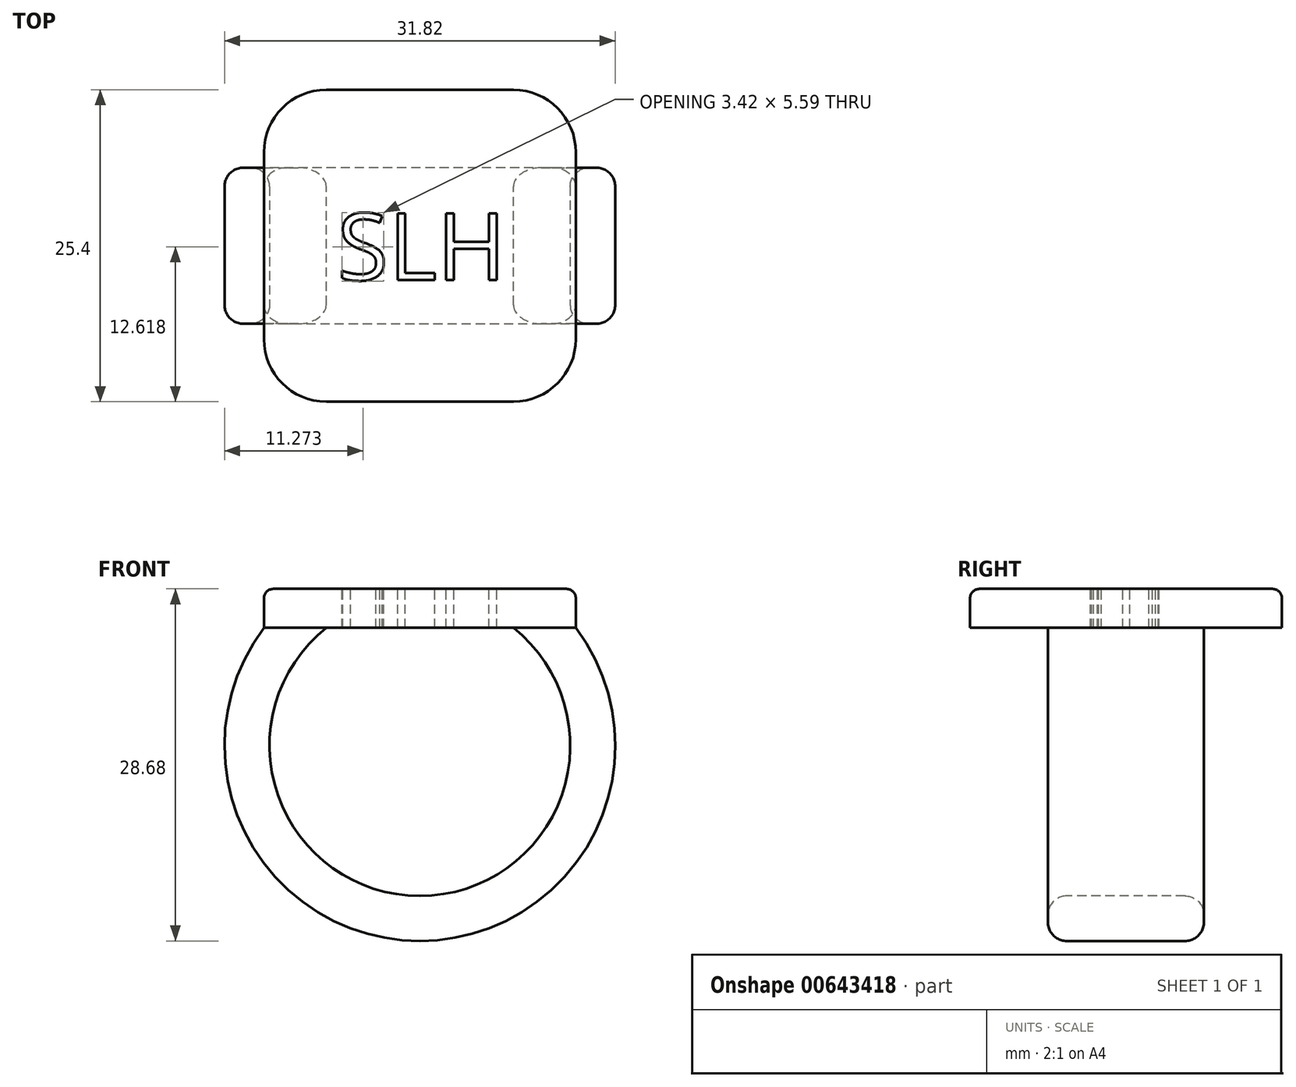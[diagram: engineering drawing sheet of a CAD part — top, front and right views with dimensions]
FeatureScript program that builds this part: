
annotation { "Feature Type Name" : "Feature", "Feature Type Description" : "" }
export const myFeature = defineFeature(function(context is Context, id is Id, definition is map)
    precondition{}
    {
        {
            var Q0;
            Q0=qCreatedBy(makeId("Top.planeOp"),FACE);
            var sketch = newSketch(context, id + "F0", { "sketchPlane" : qUnion([Q0])});
            skLineSegment(sketch, "E0.bottom", {"start": v(-12.7, 12.7) * mm, "end": v(12.7, 12.7) * mm});
            skLineSegment(sketch, "E0.top", {"start": v(-12.7, -12.7) * mm, "end": v(12.7, -12.7) * mm});
            skLineSegment(sketch, "E0.left", {"start": v(-12.7, 12.7) * mm, "end": v(-12.7, -12.7) * mm});
            skLineSegment(sketch, "E0.right", {"start": v(12.7, 12.7) * mm, "end": v(12.7, -12.7) * mm});
            skPoint(sketch, "E0.middle", {"position": v(0, 0) * mm});
            skSolve(sketch);
        }
        {
            var Q0;
            Q0 = qSketchRegion(id + "F0", true);
            extrude(context, id + "F1", {"entities" : qUnion([Q0]), "depth" : 3.17 * mm, "offsetDistance" : 25 * mm});
        }
        {
            var Q0;
            Q0=qCreatedBy(makeId("Front.planeOp"),FACE);
            var sketch = newSketch(context, id + "F2", { "sketchPlane" : qUnion([Q0])});
            skArc(sketch, "E1", {"start": v(-10.16, 0) * mm, "mid": v(0, -23.56) * mm, "end": v(10.16, 0) * mm});
            skSolve(sketch);
        }
        {
            var Q0;
            Q0=makeQuery(id+"F1.opExtrude","CAP_FACE",FACE,{"disambiguationData":[OSD([sQuery(id+"F0.wireOp",EDGE,"E0.bottom"),sQuery(id+"F0.wireOp",EDGE,"E0.top"),sQuery(id+"F0.wireOp",EDGE,"E0.left"),sQuery(id+"F0.wireOp",EDGE,"E0.right")])],"isStart":true});
            var sketch = newSketch(context, id + "F3", { "sketchPlane" : qUnion([Q0])});
            skLineSegment(sketch, "E2.bottom", {"start": v(-12.7, 6.35) * mm, "end": v(-7.62, 6.35) * mm});
            skLineSegment(sketch, "E2.top", {"start": v(-12.7, -6.35) * mm, "end": v(-7.62, -6.35) * mm});
            skLineSegment(sketch, "E2.left", {"start": v(-12.7, 6.35) * mm, "end": v(-12.7, -6.35) * mm});
            skLineSegment(sketch, "E2.right", {"start": v(-7.62, 6.35) * mm, "end": v(-7.62, -6.35) * mm});
            skPoint(sketch, "E2.middle", {"position": v(-10.16, 0) * mm});
            skSolve(sketch);
        }
        {
            var Q0;
            Q0 = qSketchRegion(id + "F3", true);
            var Q1;
            Q1 = qConstructionFilter(qBodyType(qCreatedBy(id + "F2" ,EDGE), BodyType.WIRE), ConstructionObject.NO);
            sweep(context, id + "F4", {"operationType" : NewBodyOperationType.ADD, "profiles" : qUnion([Q0]), "path" : qUnion([Q1])});
        }
        {
            var Q0;
            Q0=qCreatedBy(makeId("Front.planeOp"),FACE);
            var sketch = newSketch(context, id + "F5", { "sketchPlane" : qUnion([Q0])});
            skLineSegment(sketch, "E3.1", {"start": v(10.01, -2.54) * mm, "end": v(10.16, 0) * mm});
            skArc(sketch, "E3.2", {"start": v(10.01, -2.54) * mm, "mid": v(8.9, -1.18) * mm, "end": v(7.62, 0) * mm});
            skLineSegment(sketch, "E4.trimOffspring", {"start": v(7.62, 0) * mm, "end": v(10.16, 0) * mm});
            skPoint(sketch, "E5.0.3.start.orphan", {"position": v(-12.7, 3.18) * mm});
            skPoint(sketch, "E5.0.1.end.orphan", {"position": v(12.7, 3.18) * mm});
            skPoint(sketch, "E6.orphan", {"position": v(12.7, 0) * mm});
            skPoint(sketch, "E3.0.end.orphan", {"position": v(-7.62, 0) * mm});
            skPoint(sketch, "E3.0.start.orphan", {"position": v(-12.7, 0) * mm});
            skSolve(sketch);
        }
        {
            var Q0;
            Q0 = qSketchRegion(id + "F5", true);
            var Q1;
            Q1=makeQuery(id+"F4.opSweep","SWEPT_FACE",FACE,{"disambiguationData":[OSD([sQuery(id+"F2.wireOp",EDGE,"E1"),sQuery(id+"F3.wireOp",EDGE,"E2.bottom")])]});
            var Q2;
            Q2=makeQuery(id+"F4.opSweep","SWEPT_FACE",FACE,{"disambiguationData":[OSD([sQuery(id+"F2.wireOp",EDGE,"E1"),sQuery(id+"F3.wireOp",EDGE,"E2.top")])]});
            extrude(context, id + "F6", {"entities" : qUnion([Q0]), "operationType" : NewBodyOperationType.ADD, "endBound" : BoundingType.UP_TO_SURFACE, "depth" : 25.4 * mm, "endBoundEntityFace" : qUnion([Q1]), "offsetDistance" : 25.4 * mm, "hasSecondDirection" : true, "secondDirectionBound" : SecondDirectionBoundingType.UP_TO_SURFACE, "secondDirectionOppositeDirection" : true, "secondDirectionDepth" : 25.4 * mm, "secondDirectionBoundEntityFace" : qUnion([Q2])});
        }
        {
            var Q0;
            Q0=makeQuery(id+"F1.opExtrude","SWEPT_EDGE",EDGE,{"disambiguationData":[OSD([sQuery(id+"F0.wireOp",EDGE,"E0.top"),sQuery(id+"F0.wireOp",EDGE,"E0.left")])]});
            var Q1;
            Q1=makeQuery(id+"F1.opExtrude","SWEPT_EDGE",EDGE,{"disambiguationData":[OSD([sQuery(id+"F0.wireOp",EDGE,"E0.top"),sQuery(id+"F0.wireOp",EDGE,"E0.right")])]});
            var Q2;
            Q2=makeQuery(id+"F1.opExtrude","SWEPT_EDGE",EDGE,{"disambiguationData":[OSD([sQuery(id+"F0.wireOp",EDGE,"E0.bottom"),sQuery(id+"F0.wireOp",EDGE,"E0.right")])]});
            var Q3;
            Q3=makeQuery(id+"F1.opExtrude","SWEPT_EDGE",EDGE,{"disambiguationData":[OSD([sQuery(id+"F0.wireOp",EDGE,"E0.bottom"),sQuery(id+"F0.wireOp",EDGE,"E0.left")])]});
            fillet(context, id + "F7", {"entities" : qUnion([Q0, Q1, Q2, Q3]), "radius" : 5.08 * mm, "tangentPropagation" : true, "allowEdgeOverflow" : false});
        }
        {
            var Q0;
            {var subQ0=sQuery(id+"F3.wireOp",EDGE,"E2.top");var subQ1=sQuery(id+"F2.wireOp",EDGE,"E1");Q0=makeQuery(id+"F6.boolean.opBoolean","MERGE",EDGE,{"derivedFrom":[makeQuery(id+"F4.opSweep","SWEPT_EDGE",EDGE,{"disambiguationData":[OSD([subQ1,subQ0,sQuery(id+"F3.wireOp",EDGE,"E2.right")])]}),makeQuery(id+"F6.opExtrude","TWEAK_EDGE",EDGE,{"derivedFrom":[makeQuery(id+"F4.opSweep","SWEPT_FACE",FACE,{"disambiguationData":[OSD([subQ1,subQ0])]}),makeQuery(id+"F5.imprint","IMPRINT",EDGE,{"derivedFrom":sQuery(id+"F5.wireOp",EDGE,"E3.2")})]})]});}
            var Q1;
            Q1=makeQuery(id+"F4.opSweep","SWEPT_EDGE",EDGE,{"disambiguationData":[OSD([sQuery(id+"F0.wireOp",EDGE,"E0.left"),sQuery(id+"F2.wireOp",EDGE,"E1"),sQuery(id+"F3.wireOp",EDGE,"E2.top"),sQuery(id+"F3.wireOp",EDGE,"E2.left")])]});
            var Q2;
            {var subQ0=sQuery(id+"F3.wireOp",EDGE,"E2.bottom");var subQ1=sQuery(id+"F2.wireOp",EDGE,"E1");Q2=makeQuery(id+"F6.boolean.opBoolean","MERGE",EDGE,{"derivedFrom":[makeQuery(id+"F4.opSweep","SWEPT_EDGE",EDGE,{"disambiguationData":[OSD([subQ1,subQ0,sQuery(id+"F3.wireOp",EDGE,"E2.right")])]}),makeQuery(id+"F6.opExtrude","TWEAK_EDGE",EDGE,{"derivedFrom":[makeQuery(id+"F4.opSweep","SWEPT_FACE",FACE,{"disambiguationData":[OSD([subQ1,subQ0])]}),makeQuery(id+"F5.imprint","IMPRINT",EDGE,{"derivedFrom":sQuery(id+"F5.wireOp",EDGE,"E3.2")})]})]});}
            var Q3;
            Q3=makeQuery(id+"F4.opSweep","SWEPT_EDGE",EDGE,{"disambiguationData":[OSD([sQuery(id+"F0.wireOp",EDGE,"E0.left"),sQuery(id+"F2.wireOp",EDGE,"E1"),sQuery(id+"F3.wireOp",EDGE,"E2.bottom"),sQuery(id+"F3.wireOp",EDGE,"E2.left")])]});
            fillet(context, id + "F8", {"entities" : qUnion([Q0, Q1, Q2, Q3]), "radius" : 1.52 * mm, "tangentPropagation" : true, "allowEdgeOverflow" : false});
        }
        {
            var Q0;
            Q0=makeQuery(id+"F1.opExtrude","CAP_EDGE",EDGE,{"disambiguationData":[OSD([sQuery(id+"F0.wireOp",EDGE,"E0.top")])],"isStart":false});
            fillet(context, id + "F9", {"entities" : qUnion([Q0]), "radius" : 0.76 * mm, "tangentPropagation" : true, "allowEdgeOverflow" : false});
        }
        {
            var Q0;
            Q0=makeQuery(id+"F1.opExtrude","CAP_FACE",FACE,{"disambiguationData":[OSD([sQuery(id+"F0.wireOp",EDGE,"E0.bottom"),sQuery(id+"F0.wireOp",EDGE,"E0.top"),sQuery(id+"F0.wireOp",EDGE,"E0.left"),sQuery(id+"F0.wireOp",EDGE,"E0.right")])],"isStart":false});
            var sketch = newSketch(context, id + "F10", { "sketchPlane" : qUnion([Q0])});
            skText(sketch, "E7", { "text": "SLH", "fontName": "OpenSans-Regular.ttf"});
            const initialGuessF10  = {"E7": [-0.00674, -0.0028, 1, 0, 0.00548]};
            skSetInitialGuess(sketch, initialGuessF10);
            skSolve(sketch);
        }
        {
            var Q0;
            Q0 = qSketchRegion(id + "F10", true);
            extrude(context, id + "F11", {"entities" : qUnion([Q0]), "operationType" : NewBodyOperationType.REMOVE, "oppositeDirection" : true, "depth" : 12.7 * mm, "offsetDistance" : 25.4 * mm});
        }
    });
